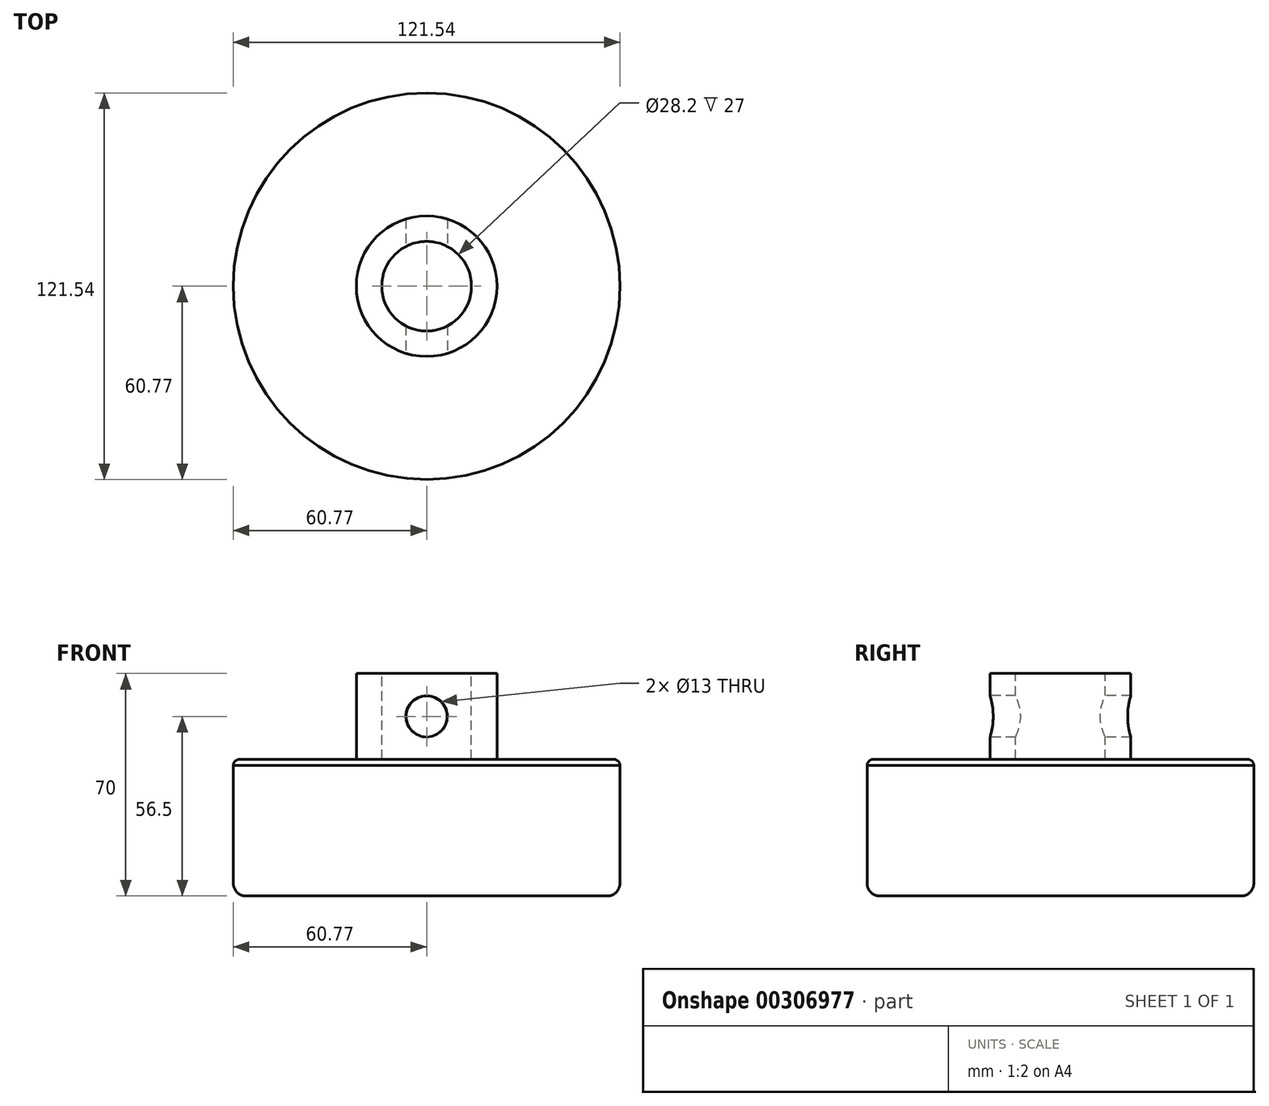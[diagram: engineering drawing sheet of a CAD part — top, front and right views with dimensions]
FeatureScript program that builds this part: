
annotation { "Feature Type Name" : "Feature", "Feature Type Description" : "" }
export const myFeature = defineFeature(function(context is Context, id is Id, definition is map)
    precondition{}
    {
        {
            var Q0;
            Q0=qCreatedBy(makeId("Front.planeOp"),FACE);
            var sketch = newSketch(context, id + "F0", { "sketchPlane" : qUnion([Q0])});
            skLineSegment(sketch, "E0", {"start": v(-14.1, 27) * mm, "end": v(-22.1, 27) * mm});
            skLineSegment(sketch, "E1", {"start": v(-22.1, 27) * mm, "end": v(-22.1, 0) * mm});
            skLineSegment(sketch, "E2", {"start": v(-58.77, 0) * mm, "end": v(-22.1, 0) * mm});
            skLineSegment(sketch, "E3", {"start": v(-60.77, -1.95) * mm, "end": v(-60.79, -2.5) * mm});
            skLineSegment(sketch, "E4", {"start": v(-60.4, -39) * mm, "end": v(-60.4, -39) * mm});
            skLineSegment(sketch, "E5", {"start": v(-56.4, -43) * mm, "end": v(0, -43) * mm});
            skPoint(sketch, "E6.end.orphan", {"position": v(0, -20) * mm});
            skPoint(sketch, "E7.visualSharp", {"position": v(-60.73, 0) * mm});
            skArc(sketch, "E7.filletArc", {"start": v(-58.77, 0) * mm, "mid": v(-60.17, -0.57) * mm, "end": v(-60.77, -1.95) * mm});
            skPoint(sketch, "E8.visualSharp", {"position": v(-60.4, -43) * mm});
            skArc(sketch, "E8.filletArc", {"start": v(-60.4, -39.16) * mm, "mid": v(-59.17, -41.88) * mm, "end": v(-56.4, -43) * mm});
            skLineSegment(sketch, "E9.top", {"start": v(0, 0) * mm, "end": v(-14.1, 0) * mm});
            skLineSegment(sketch, "E9.right", {"start": v(-14.1, 27) * mm, "end": v(-14.1, 0) * mm});
            skLineSegment(sketch, "E10.trimOffspring", {"start": v(-14.1, 0) * mm, "end": v(0, 0) * mm});
            skLineSegment(sketch, "E11.trimOffspring", {"start": v(-60.78, -2.35) * mm, "end": v(-60.77, -1.95) * mm});
            skPoint(sketch, "E12.visualSharp", {"position": v(-60.79, -2.5) * mm});
            skArc(sketch, "E12.filletArc", {"start": v(-60.78, -2.35) * mm, "mid": v(-60.74, -2.45) * mm, "end": v(-60.63, -2.5) * mm});
            skPoint(sketch, "E13.visualSharp", {"position": v(-60.4, -39) * mm});
            skArc(sketch, "E13.filletArc", {"start": v(-60.25, -39) * mm, "mid": v(-60.36, -39.05) * mm, "end": v(-60.4, -39.16) * mm});
            skLineSegment(sketch, "E14", {"start": v(0, 0) * mm, "end": v(0, -43) * mm});
            skLineSegment(sketch, "E15", {"start": v(-60.38, -11.85) * mm, "end": v(-60.38, -9.65) * mm});
            skLineSegment(sketch, "E16", {"start": v(-60.38, -9.5) * mm, "end": v(-60.38, -12) * mm});
            skPoint(sketch, "E17.visualSharp", {"position": v(-60.38, -9.5) * mm});
            skArc(sketch, "E17.filletArc", {"start": v(-60.23, -9.5) * mm, "mid": v(-60.33, -9.54) * mm, "end": v(-60.38, -9.65) * mm});
            skPoint(sketch, "E18.visualSharp", {"position": v(-60.38, -12) * mm});
            skArc(sketch, "E18.filletArc", {"start": v(-60.38, -11.85) * mm, "mid": v(-60.33, -11.96) * mm, "end": v(-60.23, -12) * mm});
            skLineSegment(sketch, "E19", {"start": v(-60.77, -1.95) * mm, "end": v(-60.77, -39) * mm});
            skLineSegment(sketch, "E20", {"start": v(-56.77, -43) * mm, "end": v(-56.4, -43) * mm});
            skPoint(sketch, "E21.visualSharp", {"position": v(-60.77, -43) * mm});
            skArc(sketch, "E21.filletArc", {"start": v(-60.77, -39) * mm, "mid": v(-59.6, -41.83) * mm, "end": v(-56.77, -43) * mm});
            skSolve(sketch);
        }
        {
            var Q0;
            Q0=makeQuery(id+"F0.imprint","IMPRINT",FACE,{"disambiguationData":[TD([[makeQuery(id+"F0.imprint","IMPRINT",EDGE,{"derivedFrom":sQuery(id+"F0.wireOp",EDGE,"E0")}),1.0]])]});
            var Q1;
            Q1=makeQuery(id+"F0.imprint","IMPRINT",FACE,{"disambiguationData":[TD([[makeQuery(id+"F0.imprint","IMPRINT",EDGE,{"derivedFrom":sQuery(id+"F0.wireOp",EDGE,"E8.filletArc")}),-1.0]])]});
            var Q2;
            Q2=sQuery(id+"F0.wireOp",EDGE,"E14");
            revolve(context, id + "F1", {"surfaceOperationType" : NewSurfaceOperationType.NEW, "entities" : qUnion([Q0, Q1]), "axis" : qUnion([Q2]), "revolveType" : RevolveType.FULL});
        }
        {
            var Q0;
            Q0=qCreatedBy(makeId("Front.planeOp"),FACE);
            var sketch = newSketch(context, id + "F2", { "sketchPlane" : qUnion([Q0])});
            skLineSegment(sketch, "E22", {"start": v(0, 0) * mm, "end": v(0, 27) * mm, "construction": true});
            skCircle(sketch, "E23", {"center": v(0, 13.5) * mm, "radius": 6.5 * mm});
            skSolve(sketch);
        }
        {
            var Q0;
            Q0=makeQuery(id+"F2.imprint","IMPRINT",FACE,{"disambiguationData":[TD([[makeQuery(id+"F2.imprint","IMPRINT",EDGE,{"derivedFrom":sQuery(id+"F2.wireOp",EDGE,"E23")}),1.0]])]});
            var Q1;
            Q1=sQuery(id+"F2.wireOp",EDGE,"E22");
            var Q2;
            Q2=sQuery(id+"F2.wireOp",EDGE,"E23");
            extrude(context, id + "F3", {"entities" : qUnion([Q0]), "operationType" : NewBodyOperationType.REMOVE, "surfaceEntities" : qUnion([Q1, Q2]), "endBound" : BoundingType.SYMMETRIC, "oppositeDirection" : true, "depth" : 60 * mm});
        }
    });
